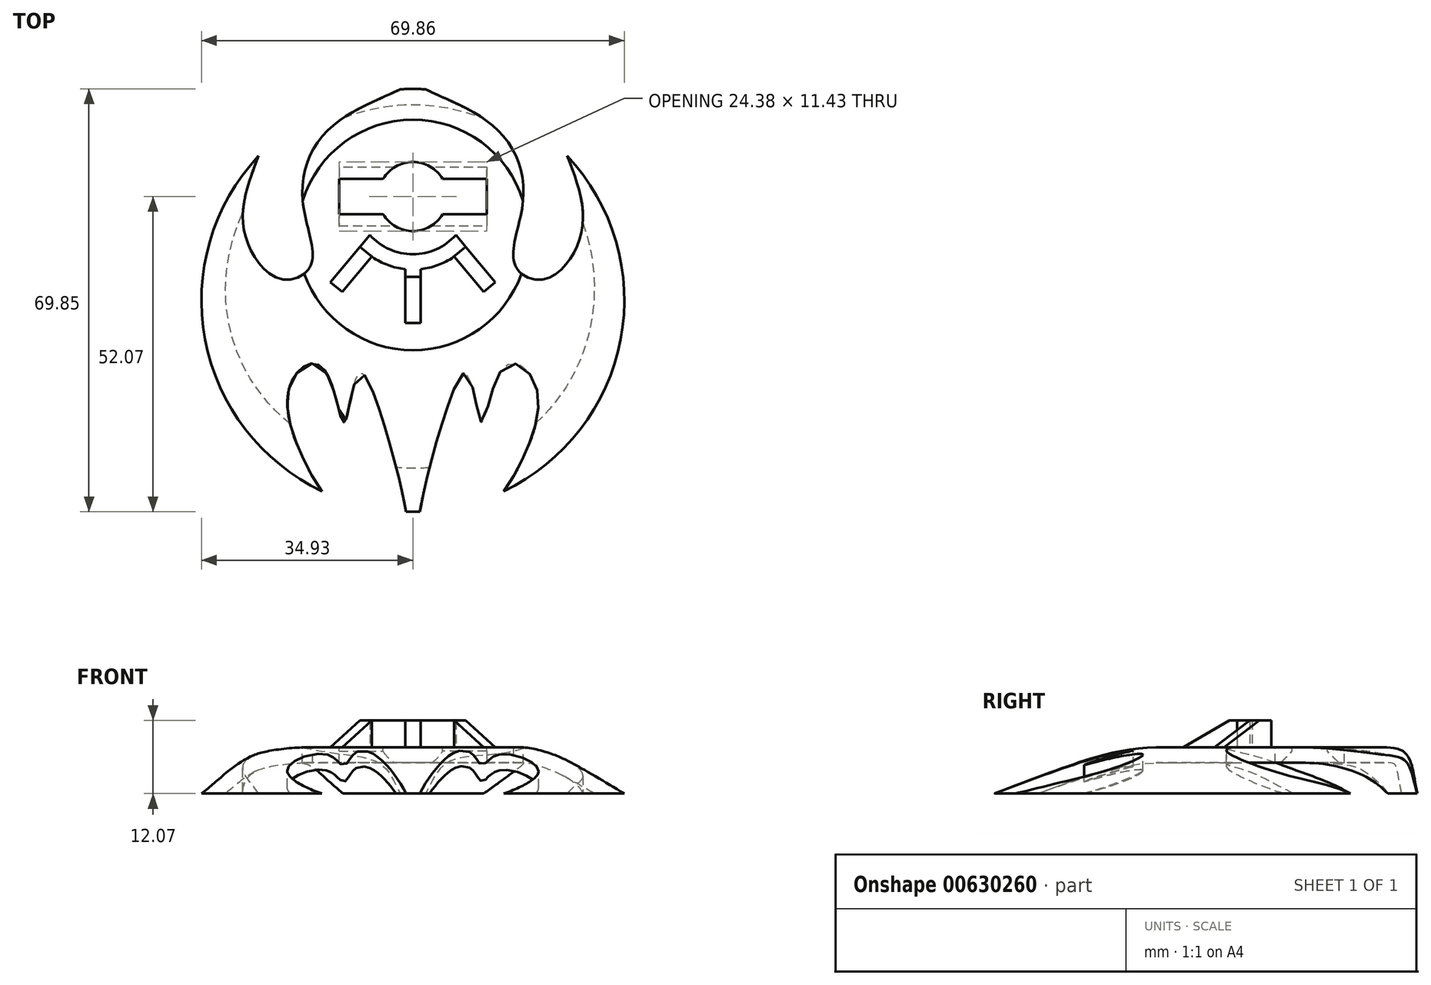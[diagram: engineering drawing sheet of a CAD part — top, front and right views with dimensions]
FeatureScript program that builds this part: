
annotation { "Feature Type Name" : "Feature", "Feature Type Description" : "" }
export const myFeature = defineFeature(function(context is Context, id is Id, definition is map)
    precondition{}
    {
        {
            var Q0;
            Q0=qCreatedBy(makeId("Top.planeOp"),FACE);
            var sketch = newSketch(context, id + "F0", { "sketchPlane" : qUnion([Q0])});
            skCircle(sketch, "E0", {"center": v(0, 0) * mm, "radius": 19.05 * mm});
            skSolve(sketch);
        }
        {
            var Q0;
            Q0=makeQuery(id+"F0.imprint","IMPRINT",FACE,{"disambiguationData":[TD([[makeQuery(id+"F0.imprint","IMPRINT",EDGE,{"derivedFrom":sQuery(id+"F0.wireOp",EDGE,"E0")}),1.0]])]});
            cPlane(context, id + "F1", {"entities" : qUnion([Q0]), "cplaneType" : CPlaneType.OFFSET, "offset" : 7.62 * mm, "oppositeDirection" : true, "width" : 152.4 * mm, "height" : 152.4 * mm});
        }
        {
            var Q0;
            Q0=qCreatedBy(id+"F1.planeOp",FACE);
            var sketch = newSketch(context, id + "F2", { "sketchPlane" : qUnion([Q0])});
            skCircle(sketch, "E1", {"center": v(0, -10.8) * mm, "radius": 34.93 * mm});
            skSolve(sketch);
        }
        {
            var Q0;
            Q0=makeQuery(id+"F0.imprint","IMPRINT",FACE,{"disambiguationData":[TD([[makeQuery(id+"F0.imprint","IMPRINT",EDGE,{"derivedFrom":sQuery(id+"F0.wireOp",EDGE,"E0")}),1.0]])]});
            var Q1;
            Q1=makeQuery(id+"F2.imprint","IMPRINT",FACE,{"disambiguationData":[TD([[makeQuery(id+"F2.imprint","IMPRINT",EDGE,{"derivedFrom":sQuery(id+"F2.wireOp",EDGE,"E1")}),1.0]])]});
            loft(context, id + "F3", {"startCondition" : LoftEndDerivativeType.TANGENT_TO_PROFILE, "startMagnitude" : 1, "sheetProfilesArray" : [{ "sheetProfileEntities" : qUnion([Q0]) }, { "sheetProfileEntities" : qUnion([Q1]) }]});
        }
        {
            var Q0;
            Q0=makeQuery(id+"F3.opLoft","CAP_FACE",FACE,{"disambiguationData":[OSD([makeQuery(id+"F2.imprint","IMPRINT",FACE,{"disambiguationData":[TD([[makeQuery(id+"F2.imprint","IMPRINT",EDGE,{"derivedFrom":sQuery(id+"F2.wireOp",EDGE,"E1")}),1.0]])]})])],"isStart":true});
            shell(context, id + "F4", {"entities" : qUnion([Q0]), "thickness" : 2.54 * mm});
        }
        {
            var Q0;
            Q0=makeQuery(id+"F3.opLoft","CAP_FACE",FACE,{"disambiguationData":[OSD([makeQuery(id+"F0.imprint","IMPRINT",FACE,{"disambiguationData":[TD([[makeQuery(id+"F0.imprint","IMPRINT",EDGE,{"derivedFrom":sQuery(id+"F0.wireOp",EDGE,"E0")}),1.0]])]})])],"isStart":true});
            var sketch = newSketch(context, id + "F5", { "sketchPlane" : qUnion([Q0])});
            skLineSegment(sketch, "E2.bottom", {"start": v(-12.2, 9.27) * mm, "end": v(-4.91, 9.27) * mm});
            skLineSegment(sketch, "E2.top", {"start": v(-12.2, 3.43) * mm, "end": v(-4.91, 3.43) * mm});
            skLineSegment(sketch, "E2.left", {"start": v(-12.2, 9.27) * mm, "end": v(-12.2, 3.43) * mm});
            skLineSegment(sketch, "E2.right", {"start": v(12.2, 9.27) * mm, "end": v(12.2, 3.43) * mm});
            skArc(sketch, "E3", {"start": v(4.91, 9.27) * mm, "mid": v(0, 12.07) * mm, "end": v(-4.91, 9.27) * mm});
            skLineSegment(sketch, "E4", {"start": v(-12.2, 6.35) * mm, "end": v(12.2, 6.35) * mm, "construction": true});
            skLineSegment(sketch, "E5", {"start": v(0, 0) * mm, "end": v(0, 19.05) * mm, "construction": true});
            skArc(sketch, "E6.trimOffspring", {"start": v(-4.91, 3.43) * mm, "mid": v(0, 0.64) * mm, "end": v(4.91, 3.43) * mm});
            skLineSegment(sketch, "E7.trimOffspring", {"start": v(4.91, 9.27) * mm, "end": v(12.2, 9.27) * mm});
            skLineSegment(sketch, "E8.trimOffspring", {"start": v(4.91, 3.43) * mm, "end": v(12.2, 3.43) * mm});
            skSolve(sketch);
        }
        {
            var Q0;
            Q0=makeQuery(id+"F5.imprint","IMPRINT",FACE,{"disambiguationData":[TD([[makeQuery(id+"F5.imprint","IMPRINT",EDGE,{"derivedFrom":sQuery(id+"F5.wireOp",EDGE,"E2.bottom")}),-1.0]])]});
            extrude(context, id + "F6", {"entities" : qUnion([Q0]), "operationType" : NewBodyOperationType.REMOVE, "oppositeDirection" : true, "depth" : 25.4 * mm, "offsetDistance" : 25.4 * mm});
        }
        {
            var Q0;
            Q0=makeQuery(id+"F3.opLoft","CAP_FACE",FACE,{"disambiguationData":[OSD([makeQuery(id+"F0.imprint","IMPRINT",FACE,{"disambiguationData":[TD([[makeQuery(id+"F0.imprint","IMPRINT",EDGE,{"derivedFrom":sQuery(id+"F0.wireOp",EDGE,"E0")}),1.0]])]})])],"isStart":true});
            var sketch = newSketch(context, id + "F7", { "sketchPlane" : qUnion([Q0])});
            skLineSegment(sketch, "E9", {"start": v(0, 0) * mm, "end": v(0, -63.75) * mm, "construction": true});
            skFitSpline(sketch, "E10", {"points": [v(25.96, 11.88) * mm, v(27.73, 0) * mm, v(21.84, -7.28) * mm, v(16.84, -4.9) * mm, v(18.2, 5.64) * mm, v(12.2, 18.87) * mm, v(0, 25.82) * mm, v(14.26, 26.27) * mm, v(25.96, 11.88) * mm]});
            skFitSpline(sketch, "E11", {"points": [v(14.15, -43.31) * mm, v(20.7, -26.74) * mm, v(15.2, -21.7) * mm, v(11.4, -30.94) * mm, v(9.1, -23.16) * mm, v(5.34, -29.5) * mm, v(1.83, -54.38) * mm, v(13.45, -43.61) * mm, v(14.15, -43.31) * mm]});
            skFitSpline(sketch, "E12.MirrorC", {"points": [v(-25.96, 11.88) * mm, v(-27.73, 0) * mm, v(-21.84, -7.28) * mm, v(-16.84, -4.9) * mm, v(-18.2, 5.64) * mm, v(-12.2, 18.87) * mm, v(0, 25.82) * mm, v(-14.26, 26.27) * mm, v(-25.96, 11.88) * mm]});
            skFitSpline(sketch, "E13.MirrorC", {"points": [v(-14.15, -43.31) * mm, v(-20.7, -26.74) * mm, v(-15.2, -21.7) * mm, v(-11.4, -30.94) * mm, v(-9.1, -23.16) * mm, v(-5.34, -29.5) * mm, v(-1.83, -54.38) * mm, v(-13.45, -43.61) * mm, v(-14.15, -43.31) * mm]});
            skSolve(sketch);
        }
        {
            var Q0;
            Q0 = qSketchRegion(id + "F7", true);
            var Q1;
            Q1=sQuery(id+"F7.wireOp",EDGE,"E11");
            var Q2;
            Q2=sQuery(id+"F7.wireOp",EDGE,"E10");
            extrude(context, id + "F8", {"entities" : qUnion([Q0]), "operationType" : NewBodyOperationType.REMOVE, "surfaceEntities" : qUnion([Q1, Q2]), "endBound" : BoundingType.THROUGH_ALL, "oppositeDirection" : true, "depth" : 25.4 * mm, "offsetDistance" : 25.4 * mm});
        }
        {
            var Q0;
            Q0=makeQuery(id+"F6.boolean.opBoolean","INTERSECT",EDGE,{"derivedFrom":[makeQuery(id+"F4.opShell","OFFSET_FACE",FACE,{"disambiguationData":[OSD([makeQuery(id+"F0.imprint","IMPRINT",FACE,{"disambiguationData":[TD([[makeQuery(id+"F0.imprint","IMPRINT",EDGE,{"derivedFrom":sQuery(id+"F0.wireOp",EDGE,"E0")}),1.0]])]})])]}),makeQuery(id+"F6.opExtrude","SWEPT_FACE",FACE,{"disambiguationData":[OSD([sQuery(id+"F5.wireOp",EDGE,"E2.top")])]})]});
            var Q1;
            Q1=makeQuery(id+"F6.boolean.opBoolean","INTERSECT",EDGE,{"derivedFrom":[makeQuery(id+"F4.opShell","OFFSET_FACE",FACE,{"disambiguationData":[OSD([makeQuery(id+"F0.imprint","IMPRINT",FACE,{"disambiguationData":[TD([[makeQuery(id+"F0.imprint","IMPRINT",EDGE,{"derivedFrom":sQuery(id+"F0.wireOp",EDGE,"E0")}),1.0]])]})])]}),makeQuery(id+"F6.opExtrude","SWEPT_FACE",FACE,{"disambiguationData":[OSD([sQuery(id+"F5.wireOp",EDGE,"E8.trimOffspring")])]})]});
            var Q2;
            Q2=makeQuery(id+"F6.boolean.opBoolean","INTERSECT",EDGE,{"derivedFrom":[makeQuery(id+"F4.opShell","OFFSET_FACE",FACE,{"disambiguationData":[OSD([makeQuery(id+"F0.imprint","IMPRINT",FACE,{"disambiguationData":[TD([[makeQuery(id+"F0.imprint","IMPRINT",EDGE,{"derivedFrom":sQuery(id+"F0.wireOp",EDGE,"E0")}),1.0]])]})])]}),makeQuery(id+"F6.opExtrude","SWEPT_FACE",FACE,{"disambiguationData":[OSD([sQuery(id+"F5.wireOp",EDGE,"E7.trimOffspring")])]})]});
            var Q3;
            Q3=makeQuery(id+"F6.boolean.opBoolean","INTERSECT",EDGE,{"derivedFrom":[makeQuery(id+"F4.opShell","OFFSET_FACE",FACE,{"disambiguationData":[OSD([makeQuery(id+"F0.imprint","IMPRINT",FACE,{"disambiguationData":[TD([[makeQuery(id+"F0.imprint","IMPRINT",EDGE,{"derivedFrom":sQuery(id+"F0.wireOp",EDGE,"E0")}),1.0]])]})])]}),makeQuery(id+"F6.opExtrude","SWEPT_FACE",FACE,{"disambiguationData":[OSD([sQuery(id+"F5.wireOp",EDGE,"E2.bottom")])]})]});
            chamfer(context, id + "F9", {"entities" : qUnion([Q0, Q1, Q2, Q3]), "width" : 1.9 * mm, "tangentPropagation" : true});
        }
        {
            var Q0;
            Q0=makeQuery(id+"F5.imprint","IMPRINT",FACE,{"disambiguationData":[TD([[makeQuery(id+"F5.imprint","IMPRINT",EDGE,{"derivedFrom":sQuery(id+"F5.wireOp",EDGE,"E2.bottom")}),1.0]])]});
            var sketch = newSketch(context, id + "F10", { "sketchPlane" : qUnion([Q0])});
            skArc(sketch, "E14", {"start": v(-7.1, 0) * mm, "mid": v(0, -3.17) * mm, "end": v(7.1, 0) * mm});
            skLineSegment(sketch, "E15", {"start": v(-1.27, -5.65) * mm, "end": v(-1.27, -14.54) * mm});
            skLineSegment(sketch, "E16", {"start": v(-1.27, -14.54) * mm, "end": v(1.27, -14.54) * mm});
            skLineSegment(sketch, "E17", {"start": v(1.27, -14.54) * mm, "end": v(1.27, -5.65) * mm});
            skLineSegment(sketch, "E18", {"start": v(-7.1, 0) * mm, "end": v(-13.63, -7.78) * mm});
            skLineSegment(sketch, "E19", {"start": v(-13.63, -7.78) * mm, "end": v(-11.68, -9.42) * mm});
            skLineSegment(sketch, "E20", {"start": v(-11.68, -9.42) * mm, "end": v(-6.8, -3.59) * mm});
            skLineSegment(sketch, "E21", {"start": v(0, 6.35) * mm, "end": v(0, -1.82) * mm, "construction": true});
            skLineSegment(sketch, "E22.MirrorCS", {"start": v(7.1, 0) * mm, "end": v(13.63, -7.78) * mm});
            skLineSegment(sketch, "E23.MirrorCS", {"start": v(11.68, -9.42) * mm, "end": v(6.8, -3.59) * mm});
            skLineSegment(sketch, "E24.MirrorCS", {"start": v(13.63, -7.78) * mm, "end": v(11.68, -9.42) * mm});
            skArc(sketch, "E25.trimOffspring", {"start": v(-6.8, -3.59) * mm, "mid": v(-4.16, -4.96) * mm, "end": v(-1.27, -5.65) * mm});
            skArc(sketch, "E26.trimOffspring", {"start": v(1.27, -5.65) * mm, "mid": v(4.16, -4.96) * mm, "end": v(6.8, -3.59) * mm});
            skSolve(sketch);
        }
        {
            var Q0;
            Q0 = qSketchRegion(id + "F10", true);
            extrude(context, id + "F11", {"entities" : qUnion([Q0]), "operationType" : NewBodyOperationType.ADD, "depth" : 4.44 * mm, "offsetDistance" : 25.4 * mm});
        }
        {
            var Q0;
            Q0=makeQuery(id+"F11.opExtrude","CAP_EDGE",EDGE,{"disambiguationData":[OSD([sQuery(id+"F10.wireOp",EDGE,"E16")])],"isStart":false});
            var Q1;
            Q1=makeQuery(id+"F11.opExtrude","CAP_EDGE",EDGE,{"disambiguationData":[OSD([sQuery(id+"F10.wireOp",EDGE,"E24.MirrorCS")])],"isStart":false});
            var Q2;
            Q2=makeQuery(id+"F11.opExtrude","CAP_EDGE",EDGE,{"disambiguationData":[OSD([sQuery(id+"F10.wireOp",EDGE,"E19")])],"isStart":false});
            chamfer(context, id + "F12", {"entities" : qUnion([Q0, Q1, Q2]), "chamferType" : ChamferType.OFFSET_ANGLE, "width" : 7.62 * mm, "oppositeDirection" : false, "angle" : 30 * degree, "tangentPropagation" : true});
        }
    });
